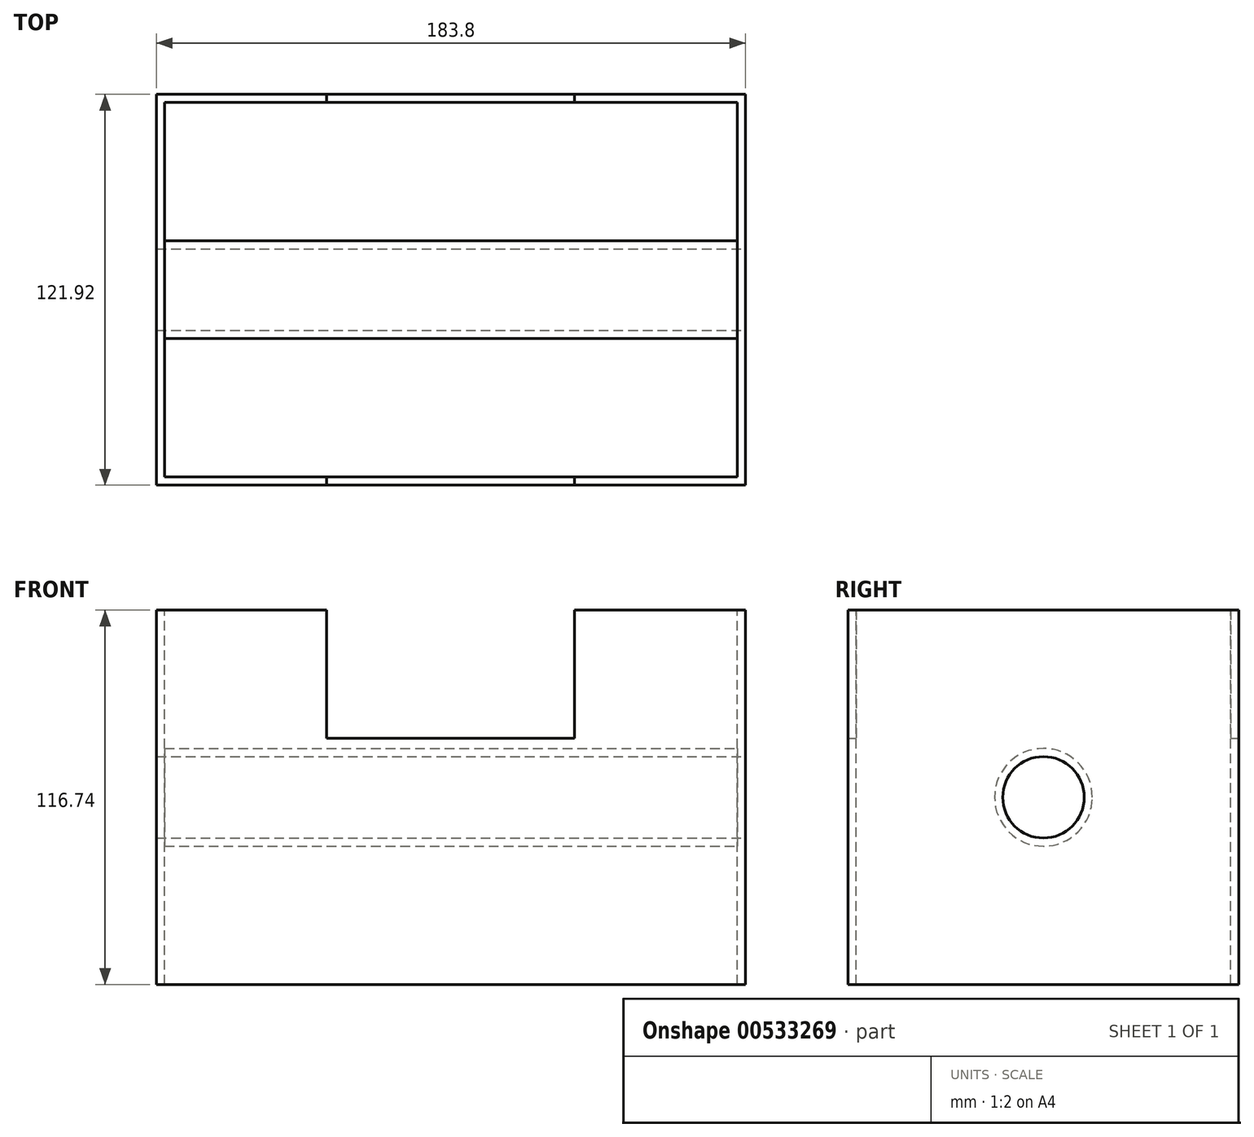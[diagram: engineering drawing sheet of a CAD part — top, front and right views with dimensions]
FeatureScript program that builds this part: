
annotation { "Feature Type Name" : "Feature", "Feature Type Description" : "" }
export const myFeature = defineFeature(function(context is Context, id is Id, definition is map)
    precondition{}
    {
        {
            var Q0;
            Q0=qCreatedBy(makeId("Front.planeOp"),FACE);
            var sketch = newSketch(context, id + "F0", { "sketchPlane" : qUnion([Q0])});
            skLineSegment(sketch, "E0.bottom", {"start": v(91.9, -58.37) * mm, "end": v(-91.9, -58.37) * mm});
            skLineSegment(sketch, "E0.top", {"start": v(91.9, 58.37) * mm, "end": v(38.78, 58.37) * mm});
            skLineSegment(sketch, "E0.left", {"start": v(91.9, -58.37) * mm, "end": v(91.9, 58.37) * mm});
            skLineSegment(sketch, "E0.right", {"start": v(-91.9, -58.37) * mm, "end": v(-91.9, 58.37) * mm});
            skPoint(sketch, "E0.middle", {"position": v(0, 0) * mm});
            skLineSegment(sketch, "E1", {"start": v(38.61, 58.37) * mm, "end": v(38.78, 58.37) * mm});
            skLineSegment(sketch, "E2.top", {"start": v(-38.78, 18.36) * mm, "end": v(38.61, 18.36) * mm});
            skLineSegment(sketch, "E2.left", {"start": v(-38.78, 58.37) * mm, "end": v(-38.78, 18.36) * mm});
            skLineSegment(sketch, "E2.right", {"start": v(38.61, 58.37) * mm, "end": v(38.61, 18.36) * mm});
            skLineSegment(sketch, "E3.trimOffspring", {"start": v(-38.78, 58.37) * mm, "end": v(-91.9, 58.37) * mm});
            skSolve(sketch);
        }
        {
            var Q0;
            Q0=makeQuery(id+"F0.imprint","IMPRINT",FACE,{"disambiguationData":[TD([[makeQuery(id+"F0.imprint","IMPRINT",EDGE,{"derivedFrom":sQuery(id+"F0.wireOp",EDGE,"E0.bottom")}),-1.0]])]});
            extrude(context, id + "F1", {"entities" : qUnion([Q0]), "endBound" : BoundingType.SYMMETRIC, "depth" : 121.92 * mm, "offsetDistance" : 25.4 * mm});
        }
        {
            var Q0;
            Q0=makeQuery(id+"F1.opExtrude","SWEPT_FACE",FACE,{"disambiguationData":[OSD([sQuery(id+"F0.wireOp",EDGE,"E0.left")])]});
            var sketch = newSketch(context, id + "F2", { "sketchPlane" : qUnion([Q0])});
            skPoint(sketch, "E4", {"position": v(0, 0) * mm});
            skSolve(sketch);
        }
        {
            var Q0;
            Q0=sQuery(id+"F2.wireOp",VERTEX,"E4");
            var Q1;
            Q1=makeQuery(id+"F1.opExtrude","SWEPT_BODY",BODY,{"disambiguationData":[OSD([sQuery(id+"F0.wireOp",EDGE,"E0.bottom"),sQuery(id+"F0.wireOp",EDGE,"E0.top"),sQuery(id+"F0.wireOp",EDGE,"E0.left"),sQuery(id+"F0.wireOp",EDGE,"E0.right"),sQuery(id+"F0.wireOp",EDGE,"E1"),sQuery(id+"F0.wireOp",EDGE,"E2.top"),sQuery(id+"F0.wireOp",EDGE,"E2.left"),sQuery(id+"F0.wireOp",EDGE,"E2.right"),sQuery(id+"F0.wireOp",EDGE,"E3.trimOffspring")])]});
            hole(context, id + "F3", {"style" : HoleStyle.SIMPLE, "endStyle" : HoleEndStyle.THROUGH, "holeDiameter" : 25.4 * mm, "isTappedThrough" : true, "tappedDepth" : 12.7 * mm, "tapClearance" : 3, "locations" : qUnion([Q0]), "scope" : qUnion([Q1])});
        }
        {
            var Q0;
            Q0=makeQuery(id+"F1.opExtrude","SWEPT_FACE",FACE,{"disambiguationData":[OSD([sQuery(id+"F0.wireOp",EDGE,"E2.right")])]});
            var Q1;
            Q1=makeQuery(id+"F1.opExtrude","SWEPT_FACE",FACE,{"disambiguationData":[OSD([sQuery(id+"F0.wireOp",EDGE,"E0.top"),sQuery(id+"F0.wireOp",EDGE,"E1")])]});
            var Q2;
            Q2=makeQuery(id+"F1.opExtrude","SWEPT_FACE",FACE,{"disambiguationData":[OSD([sQuery(id+"F0.wireOp",EDGE,"E3.trimOffspring")])]});
            var Q3;
            Q3=makeQuery(id+"F1.opExtrude","SWEPT_FACE",FACE,{"disambiguationData":[OSD([sQuery(id+"F0.wireOp",EDGE,"E2.left")])]});
            var Q4;
            Q4=makeQuery(id+"F1.opExtrude","SWEPT_FACE",FACE,{"disambiguationData":[OSD([sQuery(id+"F0.wireOp",EDGE,"E2.top")])]});
            var Q5;
            Q5=makeQuery(id+"F3.hole-0.boolean.opBoolean","COPY",FACE,{"derivedFrom":makeQuery(id+"F3.hole-0.opRevolve","SWEPT_FACE",FACE,{"disambiguationData":[OSD([sQuery(id+"F3.hole-0.sketch.wireOp",EDGE,"core_line_2")])]})});
            var Q6;
            Q6=makeQuery(id+"F1.opExtrude","SWEPT_FACE",FACE,{"disambiguationData":[OSD([sQuery(id+"F0.wireOp",EDGE,"E0.bottom")])]});
            shell(context, id + "F4", {"entities" : qUnion([Q0, Q1, Q2, Q3, Q4, Q5, Q6]), "thickness" : 2.54 * mm});
        }
    });
